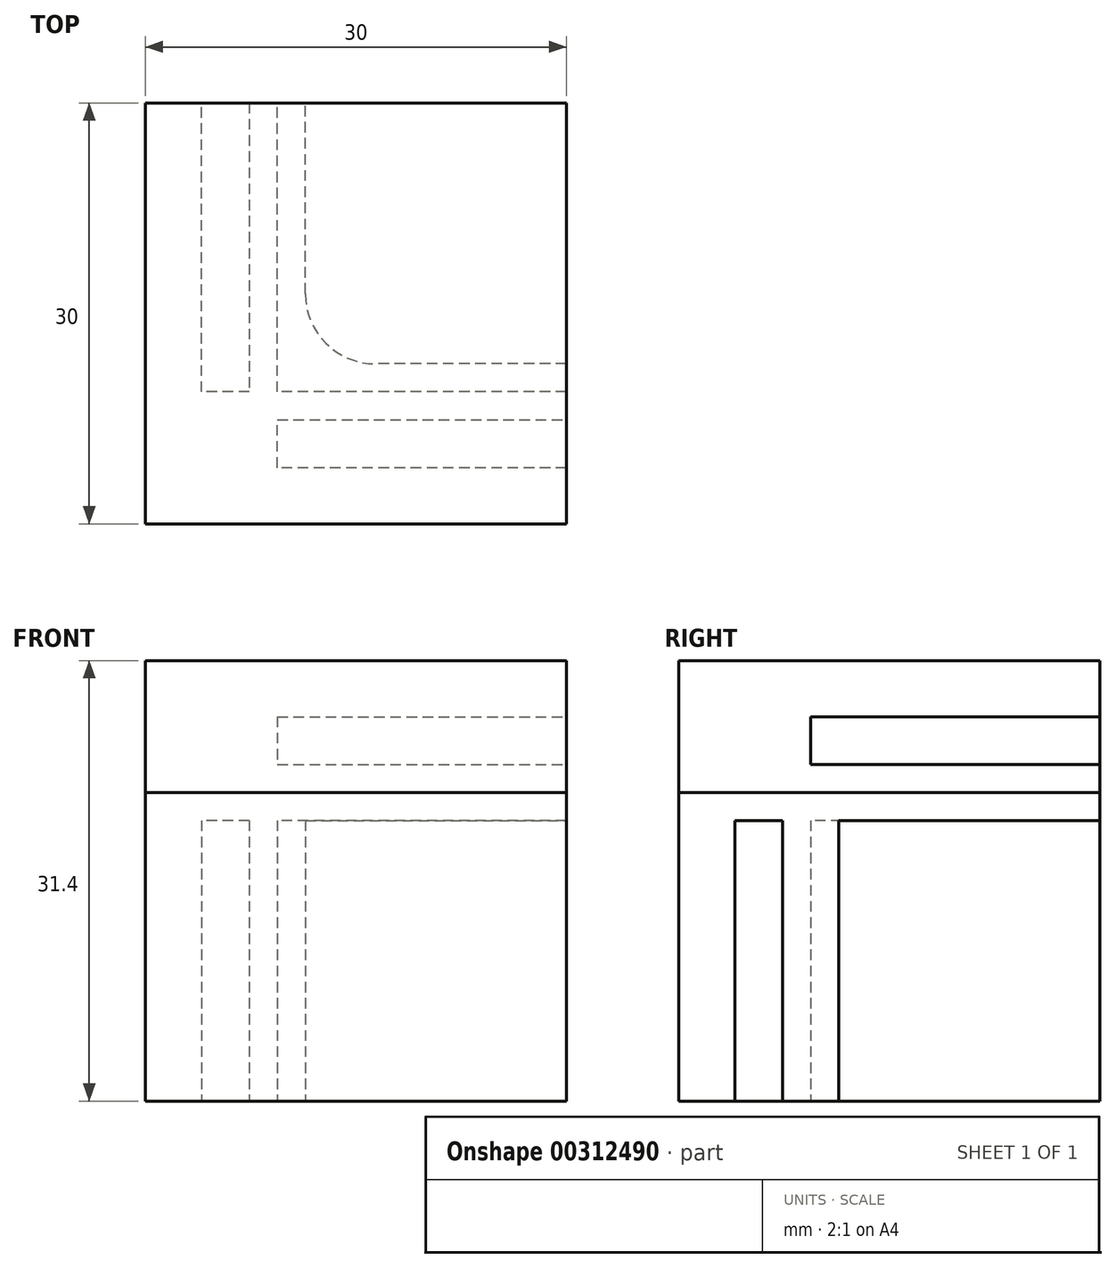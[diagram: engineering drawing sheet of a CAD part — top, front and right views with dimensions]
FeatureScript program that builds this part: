
annotation { "Feature Type Name" : "Feature", "Feature Type Description" : "" }
export const myFeature = defineFeature(function(context is Context, id is Id, definition is map)
    precondition{}
    {
        {
            assignVariable(context, id + "F0", {"name" : "a", "anyValue" : 4});
        }
        {
            assignVariable(context, id + "F1", {"name" : "b", "anyValue" : 3.4});
        }
        {
            assignVariable(context, id + "F2", {"name" : "h", "anyValue" : 30});
        }
        {
            var Q0;
            Q0=qCreatedBy(makeId("Top.planeOp"),FACE);
            var sketch = newSketch(context, id + "F3", { "sketchPlane" : qUnion([Q0])});
            skLineSegment(sketch, "E0", {"start": v(-4, 18.6) * mm, "end": v(-4, -2) * mm});
            skLineSegment(sketch, "E1", {"start": v(-4, -2) * mm, "end": v(-7.4, -2) * mm});
            skLineSegment(sketch, "E2", {"start": v(-7.4, -2) * mm, "end": v(-7.4, 18.6) * mm});
            skLineSegment(sketch, "E3", {"start": v(-7.4, 18.6) * mm, "end": v(-11.4, 18.6) * mm});
            skLineSegment(sketch, "E4", {"start": v(-11.4, 18.6) * mm, "end": v(-11.4, -11.4) * mm});
            skLineSegment(sketch, "E5", {"start": v(-11.4, -11.4) * mm, "end": v(18.6, -11.4) * mm});
            skLineSegment(sketch, "E6", {"start": v(18.6, -11.4) * mm, "end": v(18.6, -7.4) * mm});
            skLineSegment(sketch, "E7", {"start": v(18.6, -7.4) * mm, "end": v(-2, -7.4) * mm});
            skLineSegment(sketch, "E8", {"start": v(-2, -7.4) * mm, "end": v(-2, -4) * mm});
            skLineSegment(sketch, "E9", {"start": v(-2, -4) * mm, "end": v(18.6, -4) * mm});
            skLineSegment(sketch, "E10", {"start": v(18.6, -4) * mm, "end": v(18.6, 0) * mm});
            skLineSegment(sketch, "E11", {"start": v(18.6, 0) * mm, "end": v(0, 0) * mm});
            skLineSegment(sketch, "E12", {"start": v(0, 0) * mm, "end": v(0, 18.6) * mm});
            skLineSegment(sketch, "E13", {"start": v(0, 18.6) * mm, "end": v(-4, 18.6) * mm});
            skLineSegment(sketch, "E14", {"start": v(-4, -2) * mm, "end": v(-2, -2) * mm, "construction": true});
            skLineSegment(sketch, "E15", {"start": v(-2, -4) * mm, "end": v(-2, -2) * mm, "construction": true});
            skSolve(sketch);
        }
        {
            var Q0;
            Q0=makeQuery(id+"F3.imprint","IMPRINT",FACE,{"disambiguationData":[TD([[makeQuery(id+"F3.imprint","IMPRINT",EDGE,{"derivedFrom":sQuery(id+"F3.wireOp",EDGE,"E0")}),1.0]])]});
            extrude(context, id + "F4", {"entities" : qUnion([Q0]), "depth" : (getVariable(context, 'h') - 10) * mm});
        }
        {
            var Q0;
            Q0=makeQuery(id+"F4.opExtrude","CAP_FACE",FACE,{"disambiguationData":[OSD([sQuery(id+"F3.wireOp",EDGE,"E0"),sQuery(id+"F3.wireOp",EDGE,"E1"),sQuery(id+"F3.wireOp",EDGE,"E2"),sQuery(id+"F3.wireOp",EDGE,"E3"),sQuery(id+"F3.wireOp",EDGE,"E4"),sQuery(id+"F3.wireOp",EDGE,"E5"),sQuery(id+"F3.wireOp",EDGE,"E6"),sQuery(id+"F3.wireOp",EDGE,"E7"),sQuery(id+"F3.wireOp",EDGE,"E8"),sQuery(id+"F3.wireOp",EDGE,"E9"),sQuery(id+"F3.wireOp",EDGE,"E10"),sQuery(id+"F3.wireOp",EDGE,"E11"),sQuery(id+"F3.wireOp",EDGE,"E12"),sQuery(id+"F3.wireOp",EDGE,"E13")])],"isStart":false});
            var sketch = newSketch(context, id + "F5", { "sketchPlane" : qUnion([Q0])});
            skLineSegment(sketch, "E16.bottom", {"start": v(-11.4, -11.4) * mm, "end": v(18.6, -11.4) * mm});
            skLineSegment(sketch, "E16.top", {"start": v(-11.4, 18.6) * mm, "end": v(18.6, 18.6) * mm});
            skLineSegment(sketch, "E16.left", {"start": v(-11.4, -11.4) * mm, "end": v(-11.4, 18.6) * mm});
            skLineSegment(sketch, "E16.right", {"start": v(18.6, -11.4) * mm, "end": v(18.6, 18.6) * mm});
            skSolve(sketch);
        }
        {
            var Q0;
            {var subQ1=makeQuery(id+"F4.opExtrude","CAP_EDGE",EDGE,{"disambiguationData":[OSD([sQuery(id+"F3.wireOp",EDGE,"E0")])],"isStart":false});Q0=makeQuery(id+"F5.imprint","IMPRINT",FACE,{"disambiguationData":[TD([[makeQuery(id+"F5.imprint","IMPRINT",EDGE,{"derivedFrom":subQ1}),-1.0]])]});}
            var Q1;
            {var subQ4=sQuery(id+"F5.wireOp",EDGE,"E16.bottom");Q1=makeQuery(id+"F5.imprint","IMPRINT",FACE,{"disambiguationData":[TD([[makeQuery(id+"F5.imprint","IMPRINT",EDGE,{"derivedFrom":subQ4}),1.0]])]});}
            var Q2;
            {var subQ1=makeQuery(id+"F4.opExtrude","CAP_EDGE",EDGE,{"disambiguationData":[OSD([sQuery(id+"F3.wireOp",EDGE,"E7")])],"isStart":false});Q2=makeQuery(id+"F5.imprint","IMPRINT",FACE,{"disambiguationData":[TD([[makeQuery(id+"F5.imprint","IMPRINT",EDGE,{"derivedFrom":subQ1}),-1.0]])]});}
            var Q3;
            {var subQ4=makeQuery(id+"F4.opExtrude","CAP_EDGE",EDGE,{"disambiguationData":[OSD([sQuery(id+"F3.wireOp",EDGE,"E11")])],"isStart":false});Q3=makeQuery(id+"F5.imprint","IMPRINT",FACE,{"disambiguationData":[TD([[makeQuery(id+"F5.imprint","IMPRINT",EDGE,{"derivedFrom":subQ4}),-1.0]])]});}
            extrude(context, id + "F6", {"entities" : qUnion([Q0, Q1, Q2, Q3]), "operationType" : NewBodyOperationType.ADD, "depth" : (getVariable(context, 'a') / 2) * mm});
        }
        {
            var Q0;
            Q0=makeQuery(id+"F6.opExtrude","CAP_FACE",FACE,{"disambiguationData":[OSD([sQuery(id+"F5.wireOp",EDGE,"E16.bottom"),sQuery(id+"F5.wireOp",EDGE,"E16.top"),sQuery(id+"F5.wireOp",EDGE,"E16.left"),sQuery(id+"F5.wireOp",EDGE,"E16.right")])],"isStart":false});
            extrude(context, id + "F7", {"entities" : qUnion([Q0]), "depth" : (getVariable(context, 'a') / 2) * mm});
        }
        {
            var Q0;
            Q0=makeQuery(id+"F7.opExtrude","CAP_FACE",FACE,{"disambiguationData":[OSD([sQuery(id+"F5.wireOp",EDGE,"E16.bottom"),sQuery(id+"F5.wireOp",EDGE,"E16.top"),sQuery(id+"F5.wireOp",EDGE,"E16.left"),sQuery(id+"F5.wireOp",EDGE,"E16.right")])],"isStart":false});
            var sketch = newSketch(context, id + "F8", { "sketchPlane" : qUnion([Q0])});
            skLineSegment(sketch, "E17", {"start": v(-11.4, 18.6) * mm, "end": v(-11.4, -11.4) * mm});
            skLineSegment(sketch, "E18", {"start": v(-11.4, -11.4) * mm, "end": v(18.6, -11.4) * mm});
            skLineSegment(sketch, "E19", {"start": v(18.6, -11.4) * mm, "end": v(18.6, -2) * mm});
            skLineSegment(sketch, "E20", {"start": v(18.6, -2) * mm, "end": v(-2, -2) * mm});
            skLineSegment(sketch, "E21", {"start": v(-2, -2) * mm, "end": v(-2, 18.6) * mm});
            skLineSegment(sketch, "E22", {"start": v(-2, 18.6) * mm, "end": v(-11.4, 18.6) * mm});
            skLineSegment(sketch, "E23", {"start": v(-2, 18.6) * mm, "end": v(-2, -11.4) * mm});
            skPoint(sketch, "E24.0", {"position": v(-2, -2) * mm});
            skSolve(sketch);
        }
        {
            var Q0;
            Q0=makeQuery(id+"F8.imprint","IMPRINT",FACE,{"disambiguationData":[TD([[makeQuery(id+"F8.imprint","IMPRINT",EDGE,{"derivedFrom":sQuery(id+"F8.wireOp",EDGE,"E17")}),1.0]])]});
            var Q1;
            {var subQ0=sQuery(id+"F8.wireOp",EDGE,"E21");Q1=makeQuery(id+"F8.imprint","IMPRINT",FACE,{"disambiguationData":[TD([[makeQuery(id+"F8.imprint","IMPRINT",EDGE,{"derivedFrom":subQ0}),1.0]])]});}
            var Q2;
            {var subQ0=sQuery(id+"F8.wireOp",EDGE,"E19");Q2=makeQuery(id+"F8.imprint","IMPRINT",FACE,{"disambiguationData":[TD([[makeQuery(id+"F8.imprint","IMPRINT",EDGE,{"derivedFrom":subQ0}),1.0]])]});}
            extrude(context, id + "F9", {"entities" : qUnion([Q0, Q1, Q2]), "operationType" : NewBodyOperationType.ADD, "depth" : (getVariable(context, 'b')) * mm});
        }
        {
            var Q0;
            Q0=makeQuery(id+"F9.opExtrude","CAP_FACE",FACE,{"disambiguationData":[OSD([sQuery(id+"F5.wireOp",EDGE,"E16.top"),sQuery(id+"F8.wireOp",EDGE,"E17"),sQuery(id+"F8.wireOp",EDGE,"E18"),sQuery(id+"F8.wireOp",EDGE,"E19"),sQuery(id+"F8.wireOp",EDGE,"E20"),sQuery(id+"F8.wireOp",EDGE,"E21"),sQuery(id+"F8.wireOp",EDGE,"E23")])],"isStart":false});
            var sketch = newSketch(context, id + "F10", { "sketchPlane" : qUnion([Q0])});
            skPoint(sketch, "E25.0", {"position": v(18.6, 18.6) * mm});
            skLineSegment(sketch, "E26.bottom", {"start": v(-11.4, -11.4) * mm, "end": v(18.6, -11.4) * mm});
            skLineSegment(sketch, "E26.top", {"start": v(-11.4, 18.6) * mm, "end": v(18.6, 18.6) * mm});
            skLineSegment(sketch, "E26.left", {"start": v(-11.4, -11.4) * mm, "end": v(-11.4, 18.6) * mm});
            skLineSegment(sketch, "E26.right", {"start": v(18.6, -11.4) * mm, "end": v(18.6, 18.6) * mm});
            skSolve(sketch);
        }
        {
            var Q0;
            Q0 = qSketchRegion(id + "F10", true);
            extrude(context, id + "F11", {"entities" : qUnion([Q0]), "operationType" : NewBodyOperationType.ADD, "depth" : (getVariable(context, 'a')) * mm});
        }
        {
            var Q0;
            Q0=makeQuery(id+"F4.opExtrude","SWEPT_EDGE",EDGE,{"disambiguationData":[OSD([sQuery(id+"F3.wireOp",EDGE,"E11"),sQuery(id+"F3.wireOp",EDGE,"E12")])]});
            var Q1;
            Q1=makeQuery(id+"F4.opExtrude","CAP_EDGE",EDGE,{"disambiguationData":[OSD([sQuery(id+"F3.wireOp",EDGE,"E12")])],"isStart":false});
            var Q2;
            Q2=makeQuery(id+"F4.opExtrude","CAP_EDGE",EDGE,{"disambiguationData":[OSD([sQuery(id+"F3.wireOp",EDGE,"E11")])],"isStart":false});
            fillet(context, id + "F12", {"entities" : qUnion([Q0, Q1, Q2]), "radius" : 5 * mm, "tangentPropagation" : true, "allowEdgeOverflow" : false});
        }
    });
